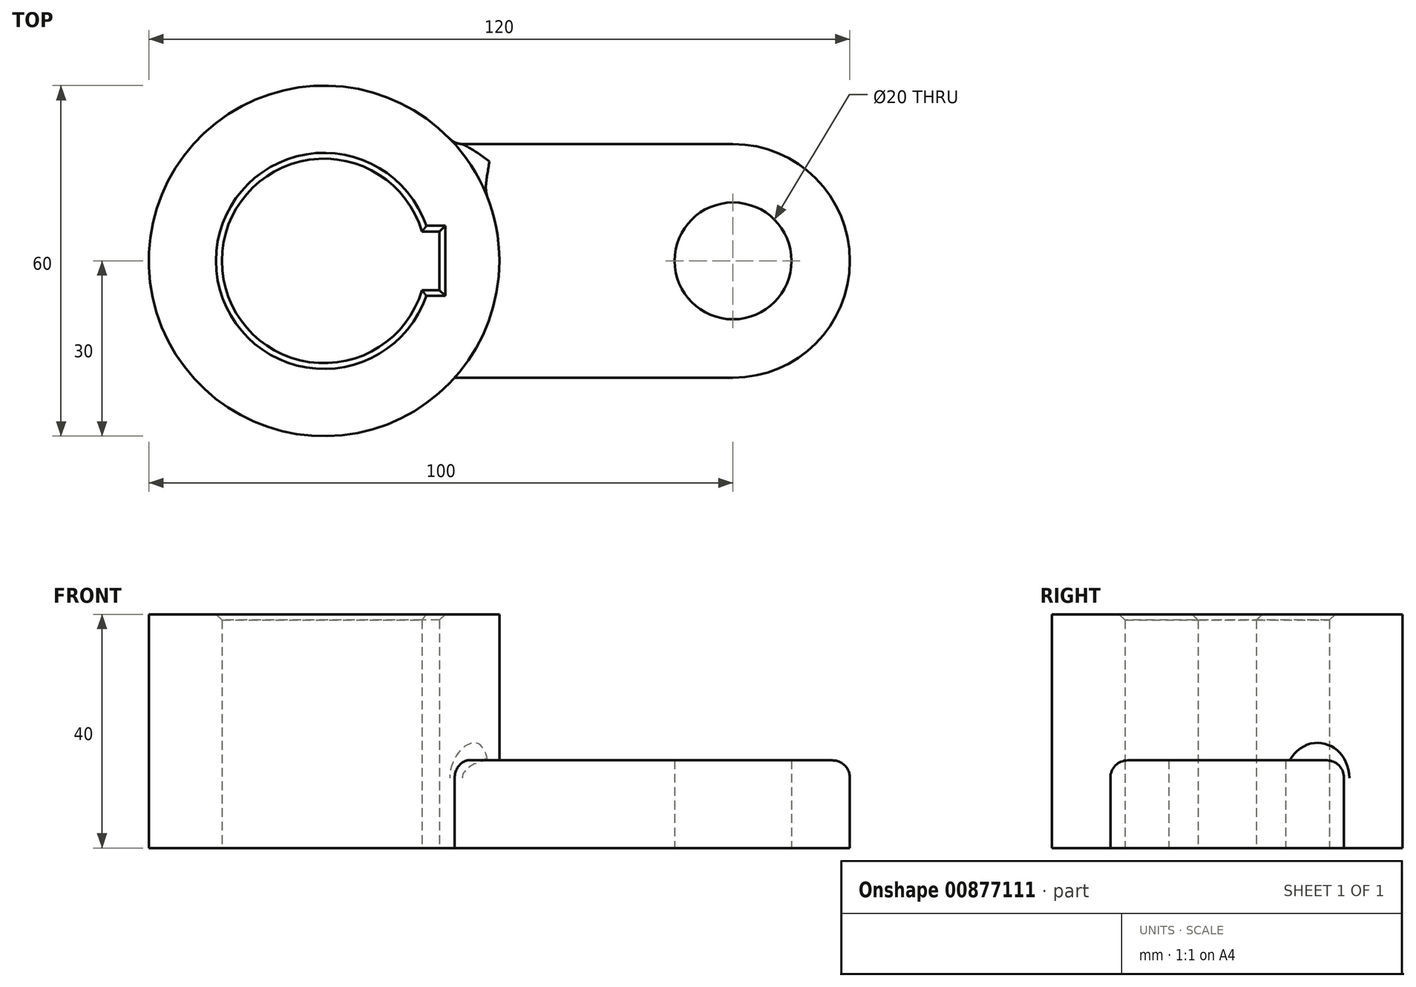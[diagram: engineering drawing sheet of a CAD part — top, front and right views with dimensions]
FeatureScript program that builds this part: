
annotation { "Feature Type Name" : "Feature", "Feature Type Description" : "" }
export const myFeature = defineFeature(function(context is Context, id is Id, definition is map)
    precondition{}
    {
        {
            var Q0;
            Q0=qCreatedBy(makeId("Top.planeOp"),FACE);
            var sketch = newSketch(context, id + "F0", { "sketchPlane" : qUnion([Q0])});
            skArc(sketch, "E0", {"start": v(22.36, 20) * mm, "mid": v(-30, 0) * mm, "end": v(22.36, -20) * mm});
            skArc(sketch, "E1", {"start": v(70, -20) * mm, "mid": v(90, 0) * mm, "end": v(70, 20) * mm});
            skLineSegment(sketch, "E2", {"start": v(70, 20) * mm, "end": v(22.36, 20) * mm});
            skLineSegment(sketch, "E3", {"start": v(70, -20) * mm, "end": v(22.36, -20) * mm});
            skCircle(sketch, "E4", {"center": v(70, 0) * mm, "radius": 10 * mm});
            skArc(sketch, "E5", {"start": v(16.77, 5) * mm, "mid": v(-17.5, 0) * mm, "end": v(16.77, -5) * mm});
            skLineSegment(sketch, "E6.bottom", {"start": v(19.77, 5) * mm, "end": v(16.77, 5) * mm});
            skLineSegment(sketch, "E6.top", {"start": v(19.77, -5) * mm, "end": v(16.77, -5) * mm});
            skLineSegment(sketch, "E6.left", {"start": v(19.77, 5) * mm, "end": v(19.77, -5) * mm});
            skSolve(sketch);
        }
        {
            var Q0;
            Q0 = qSketchRegion(id + "F0", true);
            extrude(context, id + "F1", {"entities" : qUnion([Q0]), "depth" : 15 * mm, "offsetDistance" : 25 * mm});
        }
        {
            var Q0;
            Q0=makeQuery(id+"F1.opExtrude","CAP_FACE",FACE,{"disambiguationData":[OSD([sQuery(id+"F0.wireOp",EDGE,"E0"),sQuery(id+"F0.wireOp",EDGE,"E1"),sQuery(id+"F0.wireOp",EDGE,"E2"),sQuery(id+"F0.wireOp",EDGE,"E3"),sQuery(id+"F0.wireOp",EDGE,"E4"),sQuery(id+"F0.wireOp",EDGE,"E5"),sQuery(id+"F0.wireOp",EDGE,"E6.bottom"),sQuery(id+"F0.wireOp",EDGE,"E6.top"),sQuery(id+"F0.wireOp",EDGE,"E6.left")])],"isStart":false});
            var sketch = newSketch(context, id + "F2", { "sketchPlane" : qUnion([Q0])});
            skCircle(sketch, "E7", {"center": v(0, 0) * mm, "radius": 30 * mm});
            skArc(sketch, "E8.0", {"start": v(16.77, 5) * mm, "mid": v(-17.5, 0) * mm, "end": v(16.77, -5) * mm});
            skLineSegment(sketch, "E9.0", {"start": v(19.77, 5) * mm, "end": v(19.77, -5) * mm});
            skLineSegment(sketch, "E9.1", {"start": v(19.77, 5) * mm, "end": v(16.77, 5) * mm});
            skLineSegment(sketch, "E9.2", {"start": v(19.77, -5) * mm, "end": v(16.77, -5) * mm});
            skSolve(sketch);
        }
        {
            var Q0;
            Q0 = qSketchRegion(id + "F2", true);
            extrude(context, id + "F3", {"entities" : qUnion([Q0]), "operationType" : NewBodyOperationType.ADD, "depth" : 25 * mm, "offsetDistance" : 25 * mm});
        }
        {
            var Q0;
            Q0=makeQuery(id+"F1.opExtrude","CAP_EDGE",EDGE,{"disambiguationData":[OSD([sQuery(id+"F0.wireOp",EDGE,"E1")])],"isStart":false});
            var Q1;
            Q1=makeQuery(id+"F1.opExtrude","SWEPT_EDGE",EDGE,{"disambiguationData":[OSD([sQuery(id+"F0.wireOp",EDGE,"E0"),sQuery(id+"F0.wireOp",EDGE,"E2")])]});
            fillet(context, id + "F4", {"entities" : qUnion([Q0, Q1]), "radius" : 3 * mm, "tangentPropagation" : true, "allowEdgeOverflow" : false});
        }
        {
            var Q0;
            Q0=makeQuery(id+"F3.opExtrude","CAP_EDGE",EDGE,{"disambiguationData":[OSD([sQuery(id+"F2.wireOp",EDGE,"E8.0")])],"isStart":false});
            var Q1;
            Q1=makeQuery(id+"F3.opExtrude","CAP_EDGE",EDGE,{"disambiguationData":[OSD([sQuery(id+"F2.wireOp",EDGE,"E9.1")])],"isStart":false});
            var Q2;
            Q2=makeQuery(id+"F3.opExtrude","CAP_EDGE",EDGE,{"disambiguationData":[OSD([sQuery(id+"F2.wireOp",EDGE,"E9.0")])],"isStart":false});
            var Q3;
            Q3=makeQuery(id+"F3.opExtrude","CAP_EDGE",EDGE,{"disambiguationData":[OSD([sQuery(id+"F2.wireOp",EDGE,"E9.2")])],"isStart":false});
            chamfer(context, id + "F5", {"entities" : qUnion([Q0, Q1, Q2, Q3]), "width" : 1 * mm, "tangentPropagation" : true});
        }
    });
